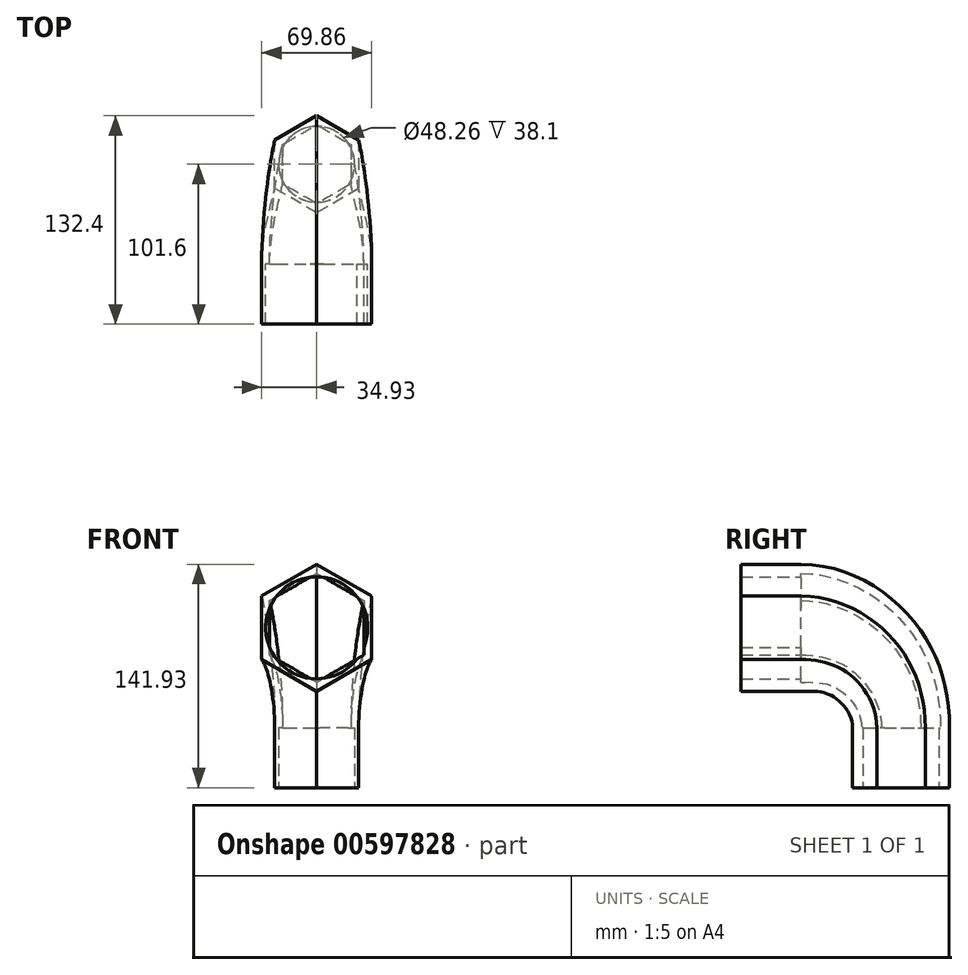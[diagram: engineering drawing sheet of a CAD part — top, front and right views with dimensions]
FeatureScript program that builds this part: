
annotation { "Feature Type Name" : "Feature", "Feature Type Description" : "" }
export const myFeature = defineFeature(function(context is Context, id is Id, definition is map)
    precondition{}
    {
        {
            var Q0;
            Q0=qCreatedBy(makeId("Front.planeOp"),FACE);
            var sketch = newSketch(context, id + "F0", { "sketchPlane" : qUnion([Q0])});
            skLineSegment(sketch, "E0", {"start": v(0, 50.8) * mm, "end": v(0, -50.8) * mm, "construction": true});
            skLineSegment(sketch, "E1", {"start": v(-50.8, 0) * mm, "end": v(50.8, 0) * mm, "construction": true});
            skCircle(sketch, "E2.cCircle", {"center": v(0, 0) * mm, "radius": 34.93 * mm, "construction": true});
            skLineSegment(sketch, "E2.0", {"start": v(0, 40.33) * mm, "end": v(34.93, 20.16) * mm});
            skLineSegment(sketch, "E2.1", {"start": v(34.92, 20.16) * mm, "end": v(34.93, -20.16) * mm});
            skLineSegment(sketch, "E2.2", {"start": v(34.93, -20.16) * mm, "end": v(0, -40.33) * mm});
            skLineSegment(sketch, "E2.3", {"start": v(0, -40.33) * mm, "end": v(-34.92, -20.16) * mm});
            skLineSegment(sketch, "E2.4", {"start": v(-34.92, -20.16) * mm, "end": v(-34.93, 20.16) * mm});
            skLineSegment(sketch, "E2.5", {"start": v(-34.93, 20.16) * mm, "end": v(0, 40.33) * mm});
            skPoint(sketch, "E2.0.midPoint", {"position": v(17.46, 30.25) * mm});
            skSolve(sketch);
        }
        {
            var Q0;
            Q0=qCreatedBy(makeId("Top.planeOp"),FACE);
            cPlane(context, id + "F1", {"entities" : qUnion([Q0]), "cplaneType" : CPlaneType.OFFSET, "offset" : 63.5 * mm, "oppositeDirection" : true, "width" : 152.4 * mm, "height" : 152.4 * mm});
        }
        {
            var Q0;
            Q0=qCreatedBy(makeId("Right.planeOp"),FACE);
            var sketch = newSketch(context, id + "F2", { "sketchPlane" : qUnion([Q0])});
            skLineSegment(sketch, "E3", {"start": v(-59.24, 0) * mm, "end": v(0, 0) * mm, "construction": true});
            skArc(sketch, "E4", {"start": v(0, 0) * mm, "mid": v(44.9, -18.6) * mm, "end": v(63.5, -63.5) * mm, "construction": true});
            skLineSegment(sketch, "E5", {"start": v(0, -63.5) * mm, "end": v(108.17, -63.5) * mm, "construction": true});
            skSolve(sketch);
        }
        {
            var Q0;
            Q0=qCreatedBy(id+"F1.planeOp",FACE);
            var sketch = newSketch(context, id + "F3", { "sketchPlane" : qUnion([Q0])});
            skPoint(sketch, "E6.0", {"position": v(0, 63.5) * mm});
            skLineSegment(sketch, "E7.0", {"start": v(0, 0) * mm, "end": v(0, 108.17) * mm, "construction": true});
            skCircle(sketch, "E8.cCircle", {"center": v(0, 63.5) * mm, "radius": 26.67 * mm, "construction": true});
            skLineSegment(sketch, "E8.0", {"start": v(26.67, 48.1) * mm, "end": v(0, 32.7) * mm});
            skLineSegment(sketch, "E8.1", {"start": v(0, 32.7) * mm, "end": v(-26.67, 48.1) * mm});
            skLineSegment(sketch, "E8.2", {"start": v(-26.67, 48.1) * mm, "end": v(-26.67, 78.9) * mm});
            skLineSegment(sketch, "E8.3", {"start": v(-26.67, 78.9) * mm, "end": v(0, 94.3) * mm});
            skLineSegment(sketch, "E8.4", {"start": v(0, 94.3) * mm, "end": v(26.67, 78.9) * mm});
            skLineSegment(sketch, "E8.5", {"start": v(26.67, 78.9) * mm, "end": v(26.67, 48.1) * mm});
            skPoint(sketch, "E8.0.midPoint", {"position": v(13.34, 40.4) * mm});
            skSolve(sketch);
        }
        {
            var Q0;
            Q0=qCreatedBy(makeId("Front.planeOp"),FACE);
            var sketch = newSketch(context, id + "F4", { "sketchPlane" : qUnion([Q0])});
            skPoint(sketch, "E9.0", {"position": v(0, -63.5) * mm});
            skLineSegment(sketch, "E10", {"start": v(-50.8, -63.5) * mm, "end": v(50.8, -63.5) * mm, "construction": true});
            skLineSegment(sketch, "E11.0", {"start": v(0, 0) * mm, "end": v(0, -63.5) * mm, "construction": true});
            skSolve(sketch);
        }
        {
            var Q0;
            Q0=sQuery(id+"F4.wireOp",EDGE,"E10");
            cPlane(context, id + "F5", {"entities" : qUnion([Q0]), "cplaneType" : CPlaneType.LINE_ANGLE, "offset" : 25.4 * mm, "angle" : 45 * degree, "oppositeDirection" : true, "width" : 152.4 * mm, "height" : 152.4 * mm});
        }
        {
            var Q0;
            Q0=qCreatedBy(id+"F5.planeOp",FACE);
            var sketch = newSketch(context, id + "F6", { "sketchPlane" : qUnion([Q0])});
            skLineSegment(sketch, "E12.0", {"start": v(0, 0) * mm, "end": v(0, 18.6) * mm});
            skCircle(sketch, "E13.cCircle", {"center": v(0, 18.6) * mm, "radius": 30.48 * mm, "construction": true});
            skLineSegment(sketch, "E13.0", {"start": v(-30.48, 36.2) * mm, "end": v(0, 53.8) * mm});
            skLineSegment(sketch, "E13.1", {"start": v(0, 53.8) * mm, "end": v(30.48, 36.2) * mm});
            skLineSegment(sketch, "E13.2", {"start": v(30.48, 36.2) * mm, "end": v(30.48, 1) * mm});
            skLineSegment(sketch, "E13.3", {"start": v(30.48, 1) * mm, "end": v(0, -16.6) * mm});
            skLineSegment(sketch, "E13.4", {"start": v(0, -16.6) * mm, "end": v(-30.48, 1) * mm});
            skLineSegment(sketch, "E13.5", {"start": v(-30.48, 1) * mm, "end": v(-30.48, 36.2) * mm});
            skPoint(sketch, "E13.0.midPoint", {"position": v(-15.24, 45) * mm});
            skLineSegment(sketch, "E14", {"start": v(0, -70.97) * mm, "end": v(0, 163.37) * mm, "construction": true});
            skSolve(sketch);
        }
        {
            var Q0;
            Q0=makeQuery(id+"F0.imprint","IMPRINT",FACE,{"disambiguationData":[TD([[makeQuery(id+"F0.imprint","IMPRINT",EDGE,{"derivedFrom":sQuery(id+"F0.wireOp",EDGE,"E2.0")}),-1.0]])]});
            var Q1;
            Q1=makeQuery(id+"F6.imprint","IMPRINT",FACE,{"disambiguationData":[TD([[makeQuery(id+"F6.imprint","IMPRINT",EDGE,{"derivedFrom":sQuery(id+"F6.wireOp",EDGE,"E13.0")}),-1.0]])]});
            var Q2;
            Q2=makeQuery(id+"F3.imprint","IMPRINT",FACE,{"disambiguationData":[TD([[makeQuery(id+"F3.imprint","IMPRINT",EDGE,{"derivedFrom":sQuery(id+"F3.wireOp",EDGE,"E8.0")}),-1.0]])]});
            loft(context, id + "F7", {"startCondition" : LoftEndDerivativeType.NORMAL_TO_PROFILE, "startMagnitude" : 1, "endCondition" : LoftEndDerivativeType.NORMAL_TO_PROFILE, "endMagnitude" : 1, "sheetProfilesArray" : [{ "sheetProfileEntities" : qUnion([Q0]) }, { "sheetProfileEntities" : qUnion([Q1]) }, { "sheetProfileEntities" : qUnion([Q2]) }]});
        }
        {
            var Q0;
            Q0=makeQuery(id+"F7.opLoft","CAP_FACE",FACE,{"disambiguationData":[OSD([makeQuery(id+"F0.imprint","IMPRINT",FACE,{"disambiguationData":[TD([[makeQuery(id+"F0.imprint","IMPRINT",EDGE,{"derivedFrom":sQuery(id+"F0.wireOp",EDGE,"E2.0")}),-1.0]])]})])],"isStart":true});
            var Q1;
            Q1=makeQuery(id+"F7.opLoft","CAP_FACE",FACE,{"disambiguationData":[OSD([makeQuery(id+"F3.imprint","IMPRINT",FACE,{"disambiguationData":[TD([[makeQuery(id+"F3.imprint","IMPRINT",EDGE,{"derivedFrom":sQuery(id+"F3.wireOp",EDGE,"E8.0")}),-1.0]])]})])],"isStart":true});
            shell(context, id + "F8", {"entities" : qUnion([Q0, Q1]), "thickness" : 5 * mm});
        }
        {
            var Q0;
            Q0=makeQuery(id+"F7.opLoft","CAP_FACE",FACE,{"disambiguationData":[OSD([makeQuery(id+"F0.imprint","IMPRINT",FACE,{"disambiguationData":[TD([[makeQuery(id+"F0.imprint","IMPRINT",EDGE,{"derivedFrom":sQuery(id+"F0.wireOp",EDGE,"E2.0")}),-1.0]])]})])],"isStart":true});
            var sketch = newSketch(context, id + "F9", { "sketchPlane" : qUnion([Q0])});
            skLineSegment(sketch, "E15.0.0", {"start": v(0, 40.33) * mm, "end": v(-34.93, 20.16) * mm});
            skLineSegment(sketch, "E15.0.1", {"start": v(-34.93, 20.16) * mm, "end": v(-34.92, -20.16) * mm});
            skLineSegment(sketch, "E15.0.2", {"start": v(-34.92, -20.16) * mm, "end": v(0, -40.33) * mm});
            skLineSegment(sketch, "E15.0.3", {"start": v(0, -40.33) * mm, "end": v(34.93, -20.16) * mm});
            skLineSegment(sketch, "E15.0.4", {"start": v(34.93, -20.16) * mm, "end": v(34.92, 20.16) * mm});
            skLineSegment(sketch, "E15.0.5", {"start": v(34.93, 20.16) * mm, "end": v(0, 40.33) * mm});
            skCircle(sketch, "E16", {"center": v(0, 0) * mm, "radius": 32.39 * mm});
            skSolve(sketch);
        }
        {
            var Q0;
            Q0=makeQuery(id+"F9.imprint","IMPRINT",FACE,{"disambiguationData":[TD([[makeQuery(id+"F9.imprint","IMPRINT",EDGE,{"derivedFrom":sQuery(id+"F9.wireOp",EDGE,"E15.0.0")}),-1.0]])]});
            var Q1;
            {var subQ0=sQuery(id+"F9.wireOp",EDGE,"E16");var subQ1=sQuery(id+"F0.wireOp",EDGE,"E2.5");var subQ2=sQuery(id+"F0.wireOp",EDGE,"E2.4");var subQ3=makeQuery(id+"F8.opShell","OFFSET_EDGE",EDGE,{"disambiguationData":[OSD([sQuery(id+"F0.wireOp",EDGE,"E2.0"),subQ2,subQ1])]});var subQ4=makeQuery(id+"F9.imprint","INTERSECT",VERTEX,{"disambiguationData":[OD(1.0)],"derivedFrom":[subQ3,subQ0]});Q1=makeQuery(id+"F9.imprint","IMPRINT",FACE,{"disambiguationData":[TD([[makeQuery(id+"F9.imprint","IMPRINT",EDGE,{"disambiguationData":[TD([[subQ4,-1.0]])],"derivedFrom":subQ0}),-1.0]])]});}
            var Q2;
            {var subQ0=sQuery(id+"F9.wireOp",EDGE,"E16");var subQ1=sQuery(id+"F0.wireOp",EDGE,"E2.5");var subQ2=sQuery(id+"F0.wireOp",EDGE,"E2.0");var subQ3=makeQuery(id+"F8.opShell","OFFSET_EDGE",EDGE,{"disambiguationData":[OSD([subQ2,sQuery(id+"F0.wireOp",EDGE,"E2.1"),subQ1])]});var subQ4=makeQuery(id+"F9.imprint","INTERSECT",VERTEX,{"disambiguationData":[OD(1.0)],"derivedFrom":[subQ3,subQ0]});Q2=makeQuery(id+"F9.imprint","IMPRINT",FACE,{"disambiguationData":[TD([[makeQuery(id+"F9.imprint","IMPRINT",EDGE,{"disambiguationData":[TD([[subQ4,-1.0]])],"derivedFrom":subQ0}),-1.0]])]});}
            var Q3;
            {var subQ0=sQuery(id+"F9.wireOp",EDGE,"E16");var subQ1=sQuery(id+"F0.wireOp",EDGE,"E2.1");var subQ2=sQuery(id+"F0.wireOp",EDGE,"E2.0");var subQ3=makeQuery(id+"F8.opShell","OFFSET_EDGE",EDGE,{"disambiguationData":[OSD([subQ2,subQ1,sQuery(id+"F0.wireOp",EDGE,"E2.5")])]});var subQ4=makeQuery(id+"F9.imprint","INTERSECT",VERTEX,{"disambiguationData":[OD(0.0)],"derivedFrom":[subQ3,subQ0]});Q3=makeQuery(id+"F9.imprint","IMPRINT",FACE,{"disambiguationData":[TD([[makeQuery(id+"F9.imprint","IMPRINT",EDGE,{"disambiguationData":[TD([[subQ4,1.0]])],"derivedFrom":subQ0}),-1.0]])]});}
            var Q4;
            {var subQ0=sQuery(id+"F9.wireOp",EDGE,"E16");var subQ1=sQuery(id+"F0.wireOp",EDGE,"E2.4");var subQ2=sQuery(id+"F0.wireOp",EDGE,"E2.3");var subQ3=makeQuery(id+"F8.opShell","OFFSET_EDGE",EDGE,{"disambiguationData":[OSD([subQ2,subQ1,sQuery(id+"F0.wireOp",EDGE,"E2.5")])]});var subQ4=makeQuery(id+"F9.imprint","INTERSECT",VERTEX,{"disambiguationData":[OD(1.0)],"derivedFrom":[subQ3,subQ0]});Q4=makeQuery(id+"F9.imprint","IMPRINT",FACE,{"disambiguationData":[TD([[makeQuery(id+"F9.imprint","IMPRINT",EDGE,{"disambiguationData":[TD([[subQ4,-1.0]])],"derivedFrom":subQ0}),-1.0]])]});}
            var Q5;
            {var subQ0=sQuery(id+"F9.wireOp",EDGE,"E16");var subQ1=sQuery(id+"F0.wireOp",EDGE,"E2.3");var subQ2=sQuery(id+"F0.wireOp",EDGE,"E2.2");var subQ3=makeQuery(id+"F8.opShell","OFFSET_EDGE",EDGE,{"disambiguationData":[OSD([subQ2,subQ1,sQuery(id+"F0.wireOp",EDGE,"E2.4")])]});var subQ4=makeQuery(id+"F9.imprint","INTERSECT",VERTEX,{"disambiguationData":[OD(1.0)],"derivedFrom":[subQ3,subQ0]});Q5=makeQuery(id+"F9.imprint","IMPRINT",FACE,{"disambiguationData":[TD([[makeQuery(id+"F9.imprint","IMPRINT",EDGE,{"disambiguationData":[TD([[subQ4,-1.0]])],"derivedFrom":subQ0}),-1.0]])]});}
            var Q6;
            {var subQ0=sQuery(id+"F9.wireOp",EDGE,"E16");var subQ1=sQuery(id+"F0.wireOp",EDGE,"E2.2");var subQ2=sQuery(id+"F0.wireOp",EDGE,"E2.1");var subQ3=makeQuery(id+"F8.opShell","OFFSET_EDGE",EDGE,{"disambiguationData":[OSD([subQ2,subQ1,sQuery(id+"F0.wireOp",EDGE,"E2.3")])]});var subQ4=makeQuery(id+"F9.imprint","INTERSECT",VERTEX,{"disambiguationData":[OD(1.0)],"derivedFrom":[subQ3,subQ0]});Q6=makeQuery(id+"F9.imprint","IMPRINT",FACE,{"disambiguationData":[TD([[makeQuery(id+"F9.imprint","IMPRINT",EDGE,{"disambiguationData":[TD([[subQ4,-1.0]])],"derivedFrom":subQ0}),-1.0]])]});}
            extrude(context, id + "F10", {"entities" : qUnion([Q0, Q1, Q2, Q3, Q4, Q5, Q6]), "operationType" : NewBodyOperationType.ADD, "depth" : 38.1 * mm, "offsetDistance" : 25.4 * mm});
        }
        {
            var Q0;
            Q0=makeQuery(id+"F7.opLoft","CAP_FACE",FACE,{"disambiguationData":[OSD([makeQuery(id+"F3.imprint","IMPRINT",FACE,{"disambiguationData":[TD([[makeQuery(id+"F3.imprint","IMPRINT",EDGE,{"derivedFrom":sQuery(id+"F3.wireOp",EDGE,"E8.0")}),-1.0]])]})])],"isStart":true});
            var sketch = newSketch(context, id + "F11", { "sketchPlane" : qUnion([Q0])});
            skLineSegment(sketch, "E17.0.0", {"start": v(26.67, -78.9) * mm, "end": v(26.67, -48.1) * mm});
            skLineSegment(sketch, "E17.0.1", {"start": v(26.67, -48.1) * mm, "end": v(0, -32.7) * mm});
            skLineSegment(sketch, "E17.0.2", {"start": v(0, -32.7) * mm, "end": v(-26.67, -48.1) * mm});
            skLineSegment(sketch, "E17.0.3", {"start": v(-26.67, -48.1) * mm, "end": v(-26.67, -78.9) * mm});
            skLineSegment(sketch, "E17.0.4", {"start": v(-26.67, -78.9) * mm, "end": v(0, -94.3) * mm});
            skLineSegment(sketch, "E17.0.5", {"start": v(0, -94.3) * mm, "end": v(26.67, -78.9) * mm});
            skSolve(sketch);
        }
        {
            var Q0;
            Q0=makeQuery(id+"F11.imprint","IMPRINT",FACE,{"disambiguationData":[TD([[makeQuery(id+"F11.imprint","IMPRINT",EDGE,{"derivedFrom":sQuery(id+"F11.wireOp",EDGE,"E17.0.0")}),1.0]])]});
            extrude(context, id + "F12", {"entities" : qUnion([Q0]), "operationType" : NewBodyOperationType.ADD, "depth" : 38.1 * mm, "offsetDistance" : 25.4 * mm});
        }
        {
            var Q0;
            Q0=makeQuery(id+"F12.opExtrude","CAP_FACE",FACE,{"disambiguationData":[OSD([sQuery(id+"F3.wireOp",EDGE,"E8.0"),sQuery(id+"F3.wireOp",EDGE,"E8.1"),sQuery(id+"F3.wireOp",EDGE,"E8.2"),sQuery(id+"F3.wireOp",EDGE,"E8.3"),sQuery(id+"F3.wireOp",EDGE,"E8.4"),sQuery(id+"F3.wireOp",EDGE,"E8.5"),sQuery(id+"F11.wireOp",EDGE,"E17.0.0"),sQuery(id+"F11.wireOp",EDGE,"E17.0.1"),sQuery(id+"F11.wireOp",EDGE,"E17.0.2"),sQuery(id+"F11.wireOp",EDGE,"E17.0.3"),sQuery(id+"F11.wireOp",EDGE,"E17.0.4"),sQuery(id+"F11.wireOp",EDGE,"E17.0.5")])],"isStart":false});
            var sketch = newSketch(context, id + "F13", { "sketchPlane" : qUnion([Q0])});
            skLineSegment(sketch, "E18", {"start": v(0, -38.48) * mm, "end": v(0, -88.52) * mm, "construction": true});
            skLineSegment(sketch, "E19", {"start": v(0, -88.52) * mm, "end": v(-21.67, -76.01) * mm, "construction": true});
            skLineSegment(sketch, "E20", {"start": v(-21.67, -76.01) * mm, "end": v(21.67, -50.99) * mm, "construction": true});
            skPoint(sketch, "E21", {"position": v(0, -63.5) * mm});
            skCircle(sketch, "E22", {"center": v(0, -63.5) * mm, "radius": 25.02 * mm});
            skSolve(sketch);
        }
        {
            var Q0;
            Q0 = qSketchRegion(id + "F13", true);
            extrude(context, id + "F14", {"entities" : qUnion([Q0]), "operationType" : NewBodyOperationType.ADD, "oppositeDirection" : true, "depth" : 38.1 * mm, "offsetDistance" : 25.4 * mm});
        }
        {
            var Q0;
            Q0=makeQuery(id+"F14.boolean.opBoolean","MERGE",FACE,{"derivedFrom":[makeQuery(id+"F12.opExtrude","CAP_FACE",FACE,{"disambiguationData":[OSD([sQuery(id+"F3.wireOp",EDGE,"E8.0"),sQuery(id+"F3.wireOp",EDGE,"E8.1"),sQuery(id+"F3.wireOp",EDGE,"E8.2"),sQuery(id+"F3.wireOp",EDGE,"E8.3"),sQuery(id+"F3.wireOp",EDGE,"E8.4"),sQuery(id+"F3.wireOp",EDGE,"E8.5"),sQuery(id+"F11.wireOp",EDGE,"E17.0.0"),sQuery(id+"F11.wireOp",EDGE,"E17.0.1"),sQuery(id+"F11.wireOp",EDGE,"E17.0.2"),sQuery(id+"F11.wireOp",EDGE,"E17.0.3"),sQuery(id+"F11.wireOp",EDGE,"E17.0.4"),sQuery(id+"F11.wireOp",EDGE,"E17.0.5")])],"isStart":false}),makeQuery(id+"F14.opExtrude","CAP_FACE",FACE,{"disambiguationData":[OSD([sQuery(id+"F13.wireOp",EDGE,"E22")])],"isStart":true})]});
            var sketch = newSketch(context, id + "F15", { "sketchPlane" : qUnion([Q0])});
            skLineSegment(sketch, "E23", {"start": v(0, -32.7) * mm, "end": v(0, -94.3) * mm, "construction": true});
            skPoint(sketch, "E24", {"position": v(0, -63.5) * mm});
            skCircle(sketch, "E25", {"center": v(0, -63.5) * mm, "radius": 24.13 * mm});
            skSolve(sketch);
        }
        {
            var Q0;
            Q0=makeQuery(id+"F15.imprint","IMPRINT",FACE,{"disambiguationData":[TD([[makeQuery(id+"F15.imprint","IMPRINT",EDGE,{"derivedFrom":sQuery(id+"F15.wireOp",EDGE,"E25")}),1.0]])]});
            extrude(context, id + "F16", {"entities" : qUnion([Q0]), "operationType" : NewBodyOperationType.REMOVE, "oppositeDirection" : true, "depth" : 38.1 * mm, "offsetDistance" : 25.4 * mm});
        }
    });
